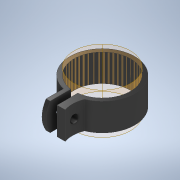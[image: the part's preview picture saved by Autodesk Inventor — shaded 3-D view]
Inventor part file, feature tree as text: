
AUTODESK INVENTOR PART (.ipt)
format: ipt  version: 2021 (Build 250183000, 183)  size: 194,560 bytes
history: native  units: mm
features: sketch x7, other x4, extrude x4, plane x1, mirror x1, split x1, revolve x1, hole x1
ambient origin geometry x8: Origin, YZ Plane, XZ Plane, XY Plane, X Axis, Y Axis, Z Axis, Center Point
bodies: Body1 (feature_tree), Body2 (feature_tree)
feature tree (20):
  other  "Sólido1"
  plane  "Plano de trabajo1"
  sketch  "Boceto3"  dims[d3=2.5mm d4=20.0mm]
  extrude  "Extrusión1"  Depth=30.0mm TaperAngle=0.0deg
  mirror  "Simetría1"
  split  "Dividir2"
  other  "Eje de trabajo1"
  revolve  "Revolución1"  [1 undecoded]
  extrude  "Extrusión2"  Depth=3.0mm TaperAngle=0.0deg
  extrude  "Extrusión3"  Depth=15.0mm
  extrude  "Extrusión4"  TaperAngle=90.0deg  [1 undecoded]
  hole  "Agujero3"  [1 undecoded]
  sketch  "Boceto1"  dims[d0=41.275mm d1=30.0mm d2=0.0mm]
  other  "Sup1"
  sketch  "Boceto5"  dims[d8=5.0mm d10=3.0mm d11=0.0mm]
  sketch  "Boceto6"  dims[d19=23.0mm d20=15.0mm]
  sketch  "Boceto8"  dims[d29=3.0mm d30=90.0deg]
  sketch  "Boceto9"  dims[d31=0.0mm d32=0.0mm d33=6.0mm]
  sketch  "Boceto10"  dims[d34=25.0mm d35=10.0mm d36=0.0mm d37=5.0mm d38=0.0mm d39=0.0mm d40=6.0mm d41=6.0mm d42=4.0mm d43=2.0mm d44=90.0deg d45=8.0mm d46=20.594885mm d47=7.5mm]
  other  "SuperficieExtrusión1"
note: 3 required parameter values undecoded (feature->parameter linkage not recoverable at this tier; creation-order binding heuristic only, values carry confidence <= 0.55)